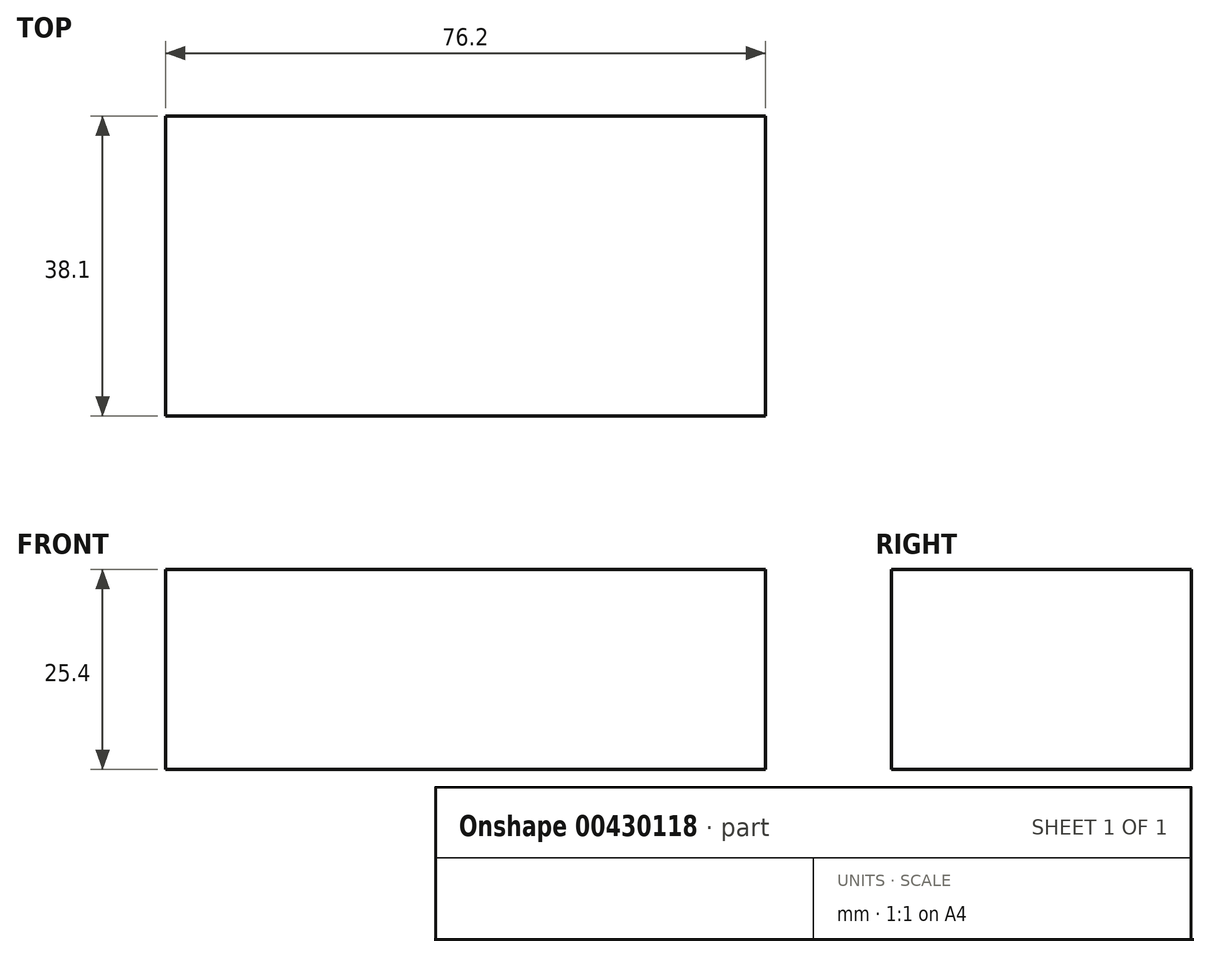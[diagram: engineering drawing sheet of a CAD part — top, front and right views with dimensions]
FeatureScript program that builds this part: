
annotation { "Feature Type Name" : "Feature", "Feature Type Description" : "" }
export const myFeature = defineFeature(function(context is Context, id is Id, definition is map)
    precondition{}
    {
        {
            var Q0;
            Q0=qCreatedBy(makeId("Top.planeOp"),FACE);
            var sketch = newSketch(context, id + "F0", { "sketchPlane" : qUnion([Q0])});
            skLineSegment(sketch, "E0.bottom", {"start": v(-34.13, 28.23) * mm, "end": v(42.07, 28.23) * mm});
            skLineSegment(sketch, "E0.top", {"start": v(-34.13, -9.87) * mm, "end": v(42.07, -9.87) * mm});
            skLineSegment(sketch, "E0.left", {"start": v(-34.13, 28.23) * mm, "end": v(-34.13, -9.87) * mm});
            skLineSegment(sketch, "E0.right", {"start": v(42.07, 28.23) * mm, "end": v(42.07, -9.87) * mm});
            skSolve(sketch);
        }
        {
            var Q0;
            Q0=makeQuery(id+"F0.imprint","IMPRINT",FACE,{"disambiguationData":[TD([[makeQuery(id+"F0.imprint","IMPRINT",EDGE,{"derivedFrom":sQuery(id+"F0.wireOp",EDGE,"E0.bottom")}),-1.0]])]});
            extrude(context, id + "F1", {"entities" : qUnion([Q0]), "depth" : 25.4 * mm});
        }
    });
